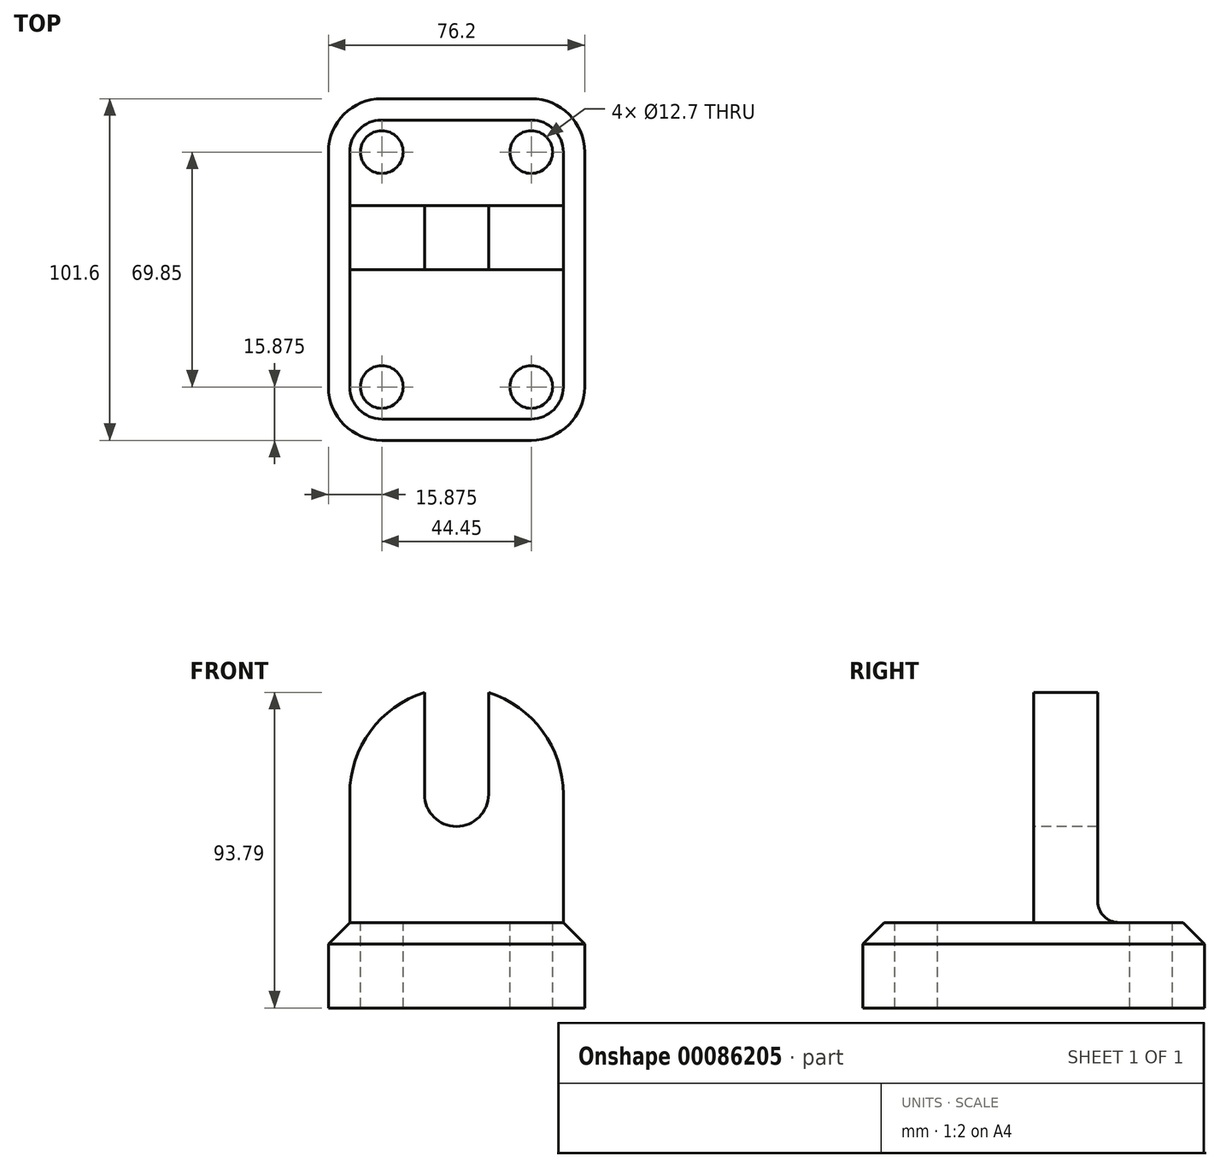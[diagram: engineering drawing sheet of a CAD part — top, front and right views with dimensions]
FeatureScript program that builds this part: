
annotation { "Feature Type Name" : "Feature", "Feature Type Description" : "" }
export const myFeature = defineFeature(function(context is Context, id is Id, definition is map)
    precondition{}
    {
        {
            var Q0;
            Q0=qCreatedBy(makeId("Top.planeOp"),FACE);
            var sketch = newSketch(context, id + "F0", { "sketchPlane" : qUnion([Q0])});
            skLineSegment(sketch, "E0.bottom", {"start": v(38.1, 50.8) * mm, "end": v(-38.1, 50.8) * mm});
            skLineSegment(sketch, "E0.top", {"start": v(38.1, -50.8) * mm, "end": v(-38.1, -50.8) * mm});
            skLineSegment(sketch, "E0.left", {"start": v(38.1, 50.8) * mm, "end": v(38.1, -50.8) * mm});
            skLineSegment(sketch, "E0.right", {"start": v(-38.1, 50.8) * mm, "end": v(-38.1, -50.8) * mm});
            skPoint(sketch, "E0.middle", {"position": v(0, 0) * mm});
            skSolve(sketch);
        }
        {
            var Q0;
            Q0=makeQuery(id+"F0.imprint","IMPRINT",FACE,{"disambiguationData":[TD([[makeQuery(id+"F0.imprint","IMPRINT",EDGE,{"derivedFrom":sQuery(id+"F0.wireOp",EDGE,"E0.bottom")}),1.0]])]});
            extrude(context, id + "F1", {"entities" : qUnion([Q0]), "depth" : 25.4 * mm});
        }
        {
            var Q0;
            Q0=makeQuery(id+"F1.opExtrude","CAP_FACE",FACE,{"disambiguationData":[OSD([sQuery(id+"F0.wireOp",EDGE,"E0.bottom"),sQuery(id+"F0.wireOp",EDGE,"E0.top"),sQuery(id+"F0.wireOp",EDGE,"E0.left"),sQuery(id+"F0.wireOp",EDGE,"E0.right")])],"isStart":false});
            var sketch = newSketch(context, id + "F2", { "sketchPlane" : qUnion([Q0])});
            skCircle(sketch, "E1", {"center": v(22.23, 34.93) * mm, "radius": 6.35 * mm});
            skCircle(sketch, "E2", {"center": v(-22.22, 34.93) * mm, "radius": 6.35 * mm});
            skCircle(sketch, "E3", {"center": v(-22.23, -34.92) * mm, "radius": 6.35 * mm});
            skLineSegment(sketch, "E4.top", {"start": v(-38.1, 0) * mm, "end": v(38.1, 0) * mm});
            skLineSegment(sketch, "E4.left", {"start": v(-38.1, -50.8) * mm, "end": v(-38.1, 0) * mm});
            skLineSegment(sketch, "E4.right", {"start": v(38.1, -50.8) * mm, "end": v(38.1, 0) * mm});
            skLineSegment(sketch, "E5.bottom", {"start": v(-38.1, 50.8) * mm, "end": v(38.1, 50.8) * mm});
            skLineSegment(sketch, "E5.top", {"start": v(-38.1, 19.05) * mm, "end": v(38.1, 19.05) * mm});
            skLineSegment(sketch, "E5.left", {"start": v(-38.1, 50.8) * mm, "end": v(-38.1, 19.05) * mm});
            skLineSegment(sketch, "E5.right", {"start": v(38.1, 50.8) * mm, "end": v(38.1, 19.05) * mm});
            skCircle(sketch, "E6", {"center": v(22.22, -34.92) * mm, "radius": 6.35 * mm});
            skLineSegment(sketch, "E7.left", {"start": v(-38.1, 19.05) * mm, "end": v(-38.1, 0) * mm});
            skLineSegment(sketch, "E7.right", {"start": v(38.1, 19.05) * mm, "end": v(38.1, 0) * mm});
            skSolve(sketch);
        }
        {
            var Q0;
            Q0=makeQuery(id+"F1.opExtrude","SWEPT_EDGE",EDGE,{"disambiguationData":[OSD([sQuery(id+"F0.wireOp",EDGE,"E0.bottom"),sQuery(id+"F0.wireOp",EDGE,"E0.left")])]});
            var Q1;
            Q1=makeQuery(id+"F1.opExtrude","SWEPT_EDGE",EDGE,{"disambiguationData":[OSD([sQuery(id+"F0.wireOp",EDGE,"E0.bottom"),sQuery(id+"F0.wireOp",EDGE,"E0.right")])]});
            var Q2;
            Q2=makeQuery(id+"F1.opExtrude","SWEPT_EDGE",EDGE,{"disambiguationData":[OSD([sQuery(id+"F0.wireOp",EDGE,"E0.top"),sQuery(id+"F0.wireOp",EDGE,"E0.right")])]});
            var Q3;
            Q3=makeQuery(id+"F1.opExtrude","SWEPT_EDGE",EDGE,{"disambiguationData":[OSD([sQuery(id+"F0.wireOp",EDGE,"E0.top"),sQuery(id+"F0.wireOp",EDGE,"E0.left")])]});
            fillet(context, id + "F3", {"entities" : qUnion([Q0, Q1, Q2, Q3]), "radius" : 15.88 * mm, "tangentPropagation" : true, "allowEdgeOverflow" : false});
        }
        {
            var Q0;
            Q0=makeQuery(id+"F1.opExtrude","CAP_FACE",FACE,{"disambiguationData":[OSD([sQuery(id+"F0.wireOp",EDGE,"E0.bottom"),sQuery(id+"F0.wireOp",EDGE,"E0.top"),sQuery(id+"F0.wireOp",EDGE,"E0.left"),sQuery(id+"F0.wireOp",EDGE,"E0.right")])],"isStart":false});
            chamfer(context, id + "F4", {"entities" : qUnion([Q0]), "width" : 6.35 * mm, "tangentPropagation" : true});
        }
        {
            var Q0;
            Q0=sQuery(id+"F2.wireOp",VERTEX,"E2.center");
            var Q1;
            Q1=sQuery(id+"F2.wireOp",VERTEX,"E1.center");
            var Q2;
            Q2=sQuery(id+"F2.wireOp",VERTEX,"E6.center");
            var Q3;
            Q3=sQuery(id+"F2.wireOp",VERTEX,"E3.center");
            var Q4;
            Q4=makeQuery(id+"F1.opExtrude","SWEPT_BODY",BODY,{"disambiguationData":[OSD([sQuery(id+"F0.wireOp",EDGE,"E0.bottom"),sQuery(id+"F0.wireOp",EDGE,"E0.top"),sQuery(id+"F0.wireOp",EDGE,"E0.left"),sQuery(id+"F0.wireOp",EDGE,"E0.right")])]});
            hole(context, id + "F5", {"style" : HoleStyle.SIMPLE, "endStyle" : HoleEndStyle.THROUGH, "holeDiameter" : 12.7 * mm, "locations" : qUnion([Q0, Q1, Q2, Q3]), "scope" : qUnion([Q4]), "isTappedThrough" : true});
        }
        {
            var Q0;
            Q0=makeQuery(id+"F2.imprint","IMPRINT",FACE,{"disambiguationData":[TD([[makeQuery(id+"F2.imprint","IMPRINT",EDGE,{"derivedFrom":sQuery(id+"F2.wireOp",EDGE,"E5.top")}),-1.0]])]});
            extrude(context, id + "F6", {"entities" : qUnion([Q0]), "operationType" : NewBodyOperationType.ADD, "depth" : 69.85 * mm});
        }
        {
            var Q0;
            Q0=makeQuery(id+"F6.opExtrude","SWEPT_FACE",FACE,{"disambiguationData":[OSD([sQuery(id+"F2.wireOp",EDGE,"E4.top")])]});
            var sketch = newSketch(context, id + "F7", { "sketchPlane" : qUnion([Q0])});
            skLineSegment(sketch, "E8.bottom", {"start": v(-31.75, 25.4) * mm, "end": v(-38.1, 25.4) * mm});
            skLineSegment(sketch, "E8.top", {"start": v(-31.75, 95.25) * mm, "end": v(-38.1, 95.25) * mm});
            skLineSegment(sketch, "E8.left", {"start": v(-31.75, 25.4) * mm, "end": v(-31.75, 95.25) * mm});
            skLineSegment(sketch, "E8.right", {"start": v(-38.1, 25.4) * mm, "end": v(-38.1, 95.25) * mm});
            skLineSegment(sketch, "E9.bottom", {"start": v(31.75, 25.4) * mm, "end": v(38.1, 25.4) * mm});
            skLineSegment(sketch, "E9.top", {"start": v(31.75, 95.25) * mm, "end": v(38.1, 95.25) * mm});
            skLineSegment(sketch, "E9.left", {"start": v(31.75, 25.4) * mm, "end": v(31.75, 95.25) * mm});
            skLineSegment(sketch, "E9.right", {"start": v(38.1, 25.4) * mm, "end": v(38.1, 95.25) * mm});
            skSolve(sketch);
        }
        {
            var Q0;
            Q0 = qSketchRegion(id + "F7", true);
            extrude(context, id + "F8", {"entities" : qUnion([Q0]), "operationType" : NewBodyOperationType.REMOVE, "oppositeDirection" : true, "depth" : 19.05 * mm});
        }
        {
            var Q0;
            Q0=makeQuery(id+"F6.opExtrude","SWEPT_FACE",FACE,{"disambiguationData":[OSD([sQuery(id+"F2.wireOp",EDGE,"E4.top")])]});
            var sketch = newSketch(context, id + "F9", { "sketchPlane" : qUnion([Q0])});
            skLineSegment(sketch, "E10", {"start": v(0, 0) * mm, "end": v(0, 63.5) * mm});
            skCircle(sketch, "E11", {"center": v(0, 63.5) * mm, "radius": 9.53 * mm});
            skCircle(sketch, "E12", {"center": v(0, 63.5) * mm, "radius": 31.75 * mm});
            skLineSegment(sketch, "E13", {"start": v(-9.53, 63.5) * mm, "end": v(-9.53, 95.25) * mm});
            skLineSegment(sketch, "E14", {"start": v(9.53, 63.5) * mm, "end": v(9.53, 95.25) * mm});
            skSolve(sketch);
        }
        {
            var Q0;
            {var subQ0=sQuery(id+"F2.wireOp",EDGE,"E4.top");Q0=makeQuery(id+"F6.boolean.opBoolean","SPLIT",EDGE,{"disambiguationData":[topologyDisambiguationEdgeConnected([makeQuery(id+"F1.opExtrude","CAP_FACE",FACE,{"disambiguationData":[OSD([sQuery(id+"F0.wireOp",EDGE,"E0.bottom"),sQuery(id+"F0.wireOp",EDGE,"E0.top"),sQuery(id+"F0.wireOp",EDGE,"E0.left"),sQuery(id+"F0.wireOp",EDGE,"E0.right")])],"isStart":false}),makeQuery(id+"F6.opExtrude","SWEPT_FACE",FACE,{"disambiguationData":[OSD([subQ0])]})])],"derivedFrom":makeQuery(id+"F6.opExtrude","CAP_EDGE",EDGE,{"disambiguationData":[OSD([subQ0])],"isStart":true})});}
            var Q1;
            {var subQ0=sQuery(id+"F2.wireOp",EDGE,"E5.top");Q1=makeQuery(id+"F6.boolean.opBoolean","SPLIT",EDGE,{"disambiguationData":[topologyDisambiguationEdgeConnected([makeQuery(id+"F1.opExtrude","CAP_FACE",FACE,{"disambiguationData":[OSD([sQuery(id+"F0.wireOp",EDGE,"E0.bottom"),sQuery(id+"F0.wireOp",EDGE,"E0.top"),sQuery(id+"F0.wireOp",EDGE,"E0.left"),sQuery(id+"F0.wireOp",EDGE,"E0.right")])],"isStart":false}),makeQuery(id+"F6.opExtrude","SWEPT_FACE",FACE,{"disambiguationData":[OSD([subQ0])]})])],"derivedFrom":makeQuery(id+"F6.opExtrude","CAP_EDGE",EDGE,{"disambiguationData":[OSD([subQ0])],"isStart":true})});}
            fillet(context, id + "F10", {"entities" : qUnion([Q0, Q1]), "radius" : 6.35 * mm, "tangentPropagation" : true, "allowEdgeOverflow" : false});
        }
        {
            var Q0;
            {var subQ0=sQuery(id+"F9.wireOp",EDGE,"E13");var subQ1=sQuery(id+"F9.wireOp",EDGE,"E12");var subQ2=makeQuery(id+"F9.imprint","INTERSECT",VERTEX,{"derivedFrom":[subQ1,subQ0]});Q0=makeQuery(id+"F9.imprint","IMPRINT",FACE,{"disambiguationData":[TD([[makeQuery(id+"F9.imprint","IMPRINT",EDGE,{"disambiguationData":[TD([[subQ2,1.0]])],"derivedFrom":subQ1}),-1.0]])]});}
            var Q1;
            {var subQ0=sQuery(id+"F9.wireOp",EDGE,"E14");var subQ1=sQuery(id+"F9.wireOp",EDGE,"E12");var subQ2=makeQuery(id+"F9.imprint","INTERSECT",VERTEX,{"derivedFrom":[subQ1,subQ0]});Q1=makeQuery(id+"F9.imprint","IMPRINT",FACE,{"disambiguationData":[TD([[makeQuery(id+"F9.imprint","IMPRINT",EDGE,{"disambiguationData":[TD([[subQ2,-1.0]])],"derivedFrom":subQ1}),-1.0]])]});}
            var Q2;
            {var subQ0=sQuery(id+"F9.wireOp",EDGE,"E13");var subQ1=sQuery(id+"F9.wireOp",EDGE,"E12");var subQ2=makeQuery(id+"F9.imprint","INTERSECT",VERTEX,{"derivedFrom":[subQ1,subQ0]});Q2=makeQuery(id+"F9.imprint","IMPRINT",FACE,{"disambiguationData":[TD([[makeQuery(id+"F9.imprint","IMPRINT",EDGE,{"disambiguationData":[TD([[subQ2,-1.0]])],"derivedFrom":subQ1}),-1.0]])]});}
            var Q3;
            {var subQ0=sQuery(id+"F9.wireOp",EDGE,"E14");var subQ1=sQuery(id+"F9.wireOp",EDGE,"E12");var subQ2=makeQuery(id+"F9.imprint","INTERSECT",VERTEX,{"derivedFrom":[subQ1,subQ0]});Q3=makeQuery(id+"F9.imprint","IMPRINT",FACE,{"disambiguationData":[TD([[makeQuery(id+"F9.imprint","IMPRINT",EDGE,{"disambiguationData":[TD([[subQ2,1.0]])],"derivedFrom":subQ1}),-1.0]])]});}
            var Q4;
            {var subQ0=sQuery(id+"F9.wireOp",EDGE,"E13");var subQ1=sQuery(id+"F9.wireOp",EDGE,"E11");var subQ2=makeQuery(id+"F9.imprint","INTERSECT",VERTEX,{"derivedFrom":[subQ1,subQ0]});Q4=makeQuery(id+"F9.imprint","IMPRINT",FACE,{"disambiguationData":[TD([[makeQuery(id+"F9.imprint","IMPRINT",EDGE,{"disambiguationData":[TD([[subQ2,1.0]])],"derivedFrom":subQ1}),-1.0]])]});}
            var Q5;
            {var subQ0=sQuery(id+"F9.wireOp",EDGE,"E11");var subQ1=makeQuery(id+"F9.imprint","INTERSECT",VERTEX,{"derivedFrom":[subQ0,sQuery(id+"F9.wireOp",EDGE,"E13")]});Q5=makeQuery(id+"F9.imprint","IMPRINT",FACE,{"disambiguationData":[TD([[makeQuery(id+"F9.imprint","IMPRINT",EDGE,{"disambiguationData":[TD([[subQ1,1.0]])],"derivedFrom":subQ0}),1.0]])]});}
            extrude(context, id + "F11", {"entities" : qUnion([Q0, Q1, Q2, Q3, Q4, Q5]), "operationType" : NewBodyOperationType.REMOVE, "oppositeDirection" : true, "depth" : 19.05 * mm});
        }
        {
            var Q0;
            {var subQ0=sQuery(id+"F9.wireOp",EDGE,"E13");var subQ1=sQuery(id+"F9.wireOp",EDGE,"E11");var subQ2=makeQuery(id+"F9.imprint","INTERSECT",VERTEX,{"derivedFrom":[subQ1,subQ0]});Q0=makeQuery(id+"F9.imprint","IMPRINT",FACE,{"disambiguationData":[TD([[makeQuery(id+"F9.imprint","IMPRINT",EDGE,{"disambiguationData":[TD([[subQ2,1.0]])],"derivedFrom":subQ1}),-1.0]])]});}
            var Q1;
            {var subQ0=sQuery(id+"F9.wireOp",EDGE,"E11");var subQ1=makeQuery(id+"F9.imprint","INTERSECT",VERTEX,{"derivedFrom":[subQ0,sQuery(id+"F9.wireOp",EDGE,"E13")]});Q1=makeQuery(id+"F9.imprint","IMPRINT",FACE,{"disambiguationData":[TD([[makeQuery(id+"F9.imprint","IMPRINT",EDGE,{"disambiguationData":[TD([[subQ1,1.0]])],"derivedFrom":subQ0}),1.0]])]});}
            extrude(context, id + "F12", {"entities" : qUnion([Q0, Q1]), "operationType" : NewBodyOperationType.REMOVE, "oppositeDirection" : true, "depth" : 19.05 * mm});
        }
    });
